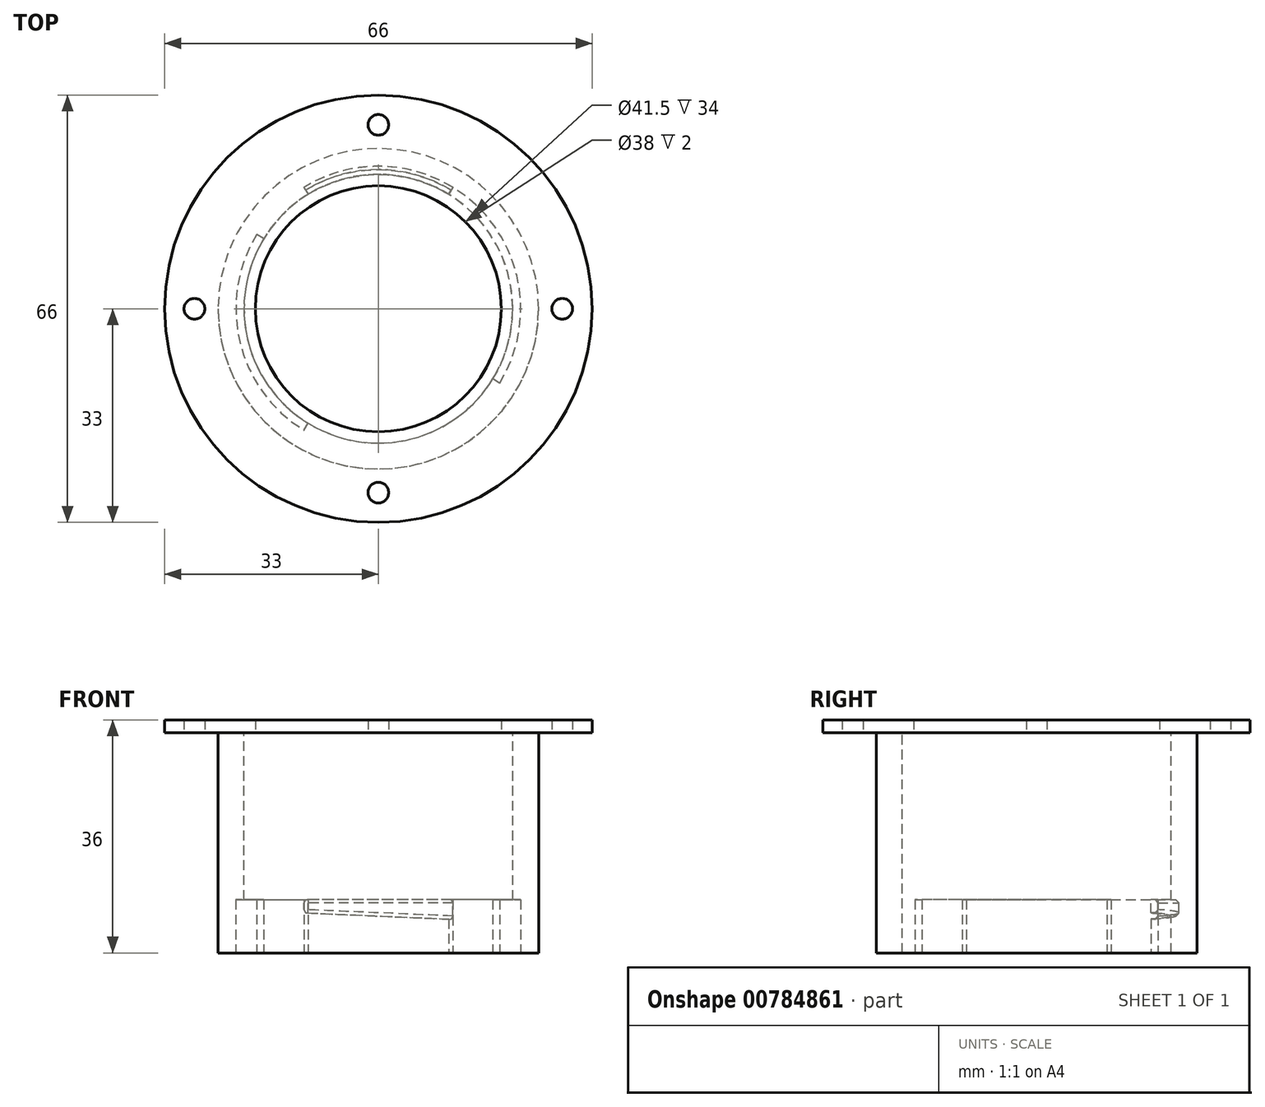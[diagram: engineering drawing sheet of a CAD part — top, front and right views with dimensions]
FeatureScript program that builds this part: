
annotation { "Feature Type Name" : "Feature", "Feature Type Description" : "" }
export const myFeature = defineFeature(function(context is Context, id is Id, definition is map)
    precondition{}
    {
        {
            var Q0;
            Q0=qCreatedBy(makeId("Top.planeOp"),FACE);
            var sketch = newSketch(context, id + "F0", { "sketchPlane" : qUnion([Q0])});
            skCircle(sketch, "E0", {"center": v(0, 0) * mm, "radius": 20.75 * mm});
            skCircle(sketch, "E1", {"center": v(0, 0) * mm, "radius": 18.75 * mm});
            skSolve(sketch);
        }
        {
            var Q0;
            Q0=makeQuery(id+"F0.imprint","IMPRINT",FACE,{"disambiguationData":[TD([[makeQuery(id+"F0.imprint","IMPRINT",EDGE,{"derivedFrom":sQuery(id+"F0.wireOp",EDGE,"E0")}),1.0]])]});
            extrude(context, id + "F1", {"entities" : qUnion([Q0]), "depth" : 34 * mm});
        }
        {
            var Q0;
            Q0=makeQuery(id+"F1.opExtrude","CAP_FACE",FACE,{"disambiguationData":[OSD([sQuery(id+"F0.wireOp",EDGE,"E0"),sQuery(id+"F0.wireOp",EDGE,"E1")])],"isStart":false});
            cPlane(context, id + "F2", {"entities" : qUnion([Q0]), "cplaneType" : CPlaneType.OFFSET, "offset" : 25.8 * mm, "oppositeDirection" : true, "width" : 150 * mm, "height" : 150 * mm});
        }
        {
            var Q0;
            Q0=qCreatedBy(id+"F2.planeOp",FACE);
            var sketch = newSketch(context, id + "F3", { "sketchPlane" : qUnion([Q0])});
            skCircle(sketch, "E2.0", {"center": v(0, 0) * mm, "radius": 20.75 * mm});
            skCircle(sketch, "E3", {"center": v(0, 0) * mm, "radius": 22 * mm});
            skLineSegment(sketch, "E4", {"start": v(-11.5, 18.75) * mm, "end": v(11.5, -18.75) * mm});
            skLineSegment(sketch, "E5", {"start": v(-11.5, -18.75) * mm, "end": v(11.5, 18.75) * mm});
            skLineSegment(sketch, "E6", {"start": v(-11.5, 18.75) * mm, "end": v(0, 21.22) * mm, "construction": true});
            skLineSegment(sketch, "E7", {"start": v(0, 21.22) * mm, "end": v(11.5, 18.75) * mm, "construction": true});
            skSolve(sketch);
        }
        {
            var Q0;
            {var subQ0=sQuery(id+"F3.wireOp",EDGE,"E4");var subQ1=sQuery(id+"F3.wireOp",EDGE,"E2.0");var subQ2=makeQuery(id+"F3.imprint","INTERSECT",VERTEX,{"disambiguationData":[OD(0.0)],"derivedFrom":[subQ1,subQ0]});Q0=makeQuery(id+"F3.imprint","IMPRINT",FACE,{"disambiguationData":[TD([[makeQuery(id+"F3.imprint","IMPRINT",EDGE,{"disambiguationData":[TD([[subQ2,1.0]])],"derivedFrom":subQ1}),-1.0]])]});}
            var Q1;
            {var subQ0=sQuery(id+"F3.wireOp",EDGE,"E5");var subQ1=sQuery(id+"F3.wireOp",EDGE,"E2.0");var subQ2=makeQuery(id+"F3.imprint","INTERSECT",VERTEX,{"disambiguationData":[OD(1.0)],"derivedFrom":[subQ1,subQ0]});Q1=makeQuery(id+"F3.imprint","IMPRINT",FACE,{"disambiguationData":[TD([[makeQuery(id+"F3.imprint","IMPRINT",EDGE,{"disambiguationData":[TD([[subQ2,-1.0]])],"derivedFrom":subQ1}),-1.0]])]});}
            extrude(context, id + "F4", {"entities" : qUnion([Q0, Q1]), "operationType" : NewBodyOperationType.ADD, "oppositeDirection" : true, "depth" : 3 * mm, "offsetDistance" : 25 * mm});
        }
        {
            var Q0;
            Q0=qCreatedBy(makeId("Front.planeOp"),FACE);
            cPlane(context, id + "F5", {"entities" : qUnion([Q0]), "cplaneType" : CPlaneType.OFFSET, "offset" : 25 * mm, "width" : 150 * mm, "height" : 150 * mm});
        }
        {
            var Q0;
            Q0=qCreatedBy(id+"F5.planeOp",FACE);
            var sketch = newSketch(context, id + "F6", { "sketchPlane" : qUnion([Q0])});
            skLineSegment(sketch, "E8.0.0", {"start": v(11.5, 8.2) * mm, "end": v(-11.5, 8.2) * mm});
            skLineSegment(sketch, "E8.0.1", {"start": v(-11.5, 8.2) * mm, "end": v(-11.5, 5.2) * mm});
            skLineSegment(sketch, "E8.0.2", {"start": v(-11.5, 5.2) * mm, "end": v(11.5, 5.2) * mm});
            skLineSegment(sketch, "E8.0.3", {"start": v(11.5, 5.2) * mm, "end": v(11.5, 8.2) * mm});
            skLineSegment(sketch, "E9", {"start": v(11.5, 6.2) * mm, "end": v(-11.5, 5.2) * mm});
            skSolve(sketch);
        }
        {
            var Q0;
            {var subQ0=sQuery(id+"F6.wireOp",EDGE,"E8.0.2");Q0=makeQuery(id+"F6.imprint","IMPRINT",FACE,{"disambiguationData":[TD([[makeQuery(id+"F6.imprint","IMPRINT",EDGE,{"derivedFrom":subQ0}),1.0]])]});}
            var Q1;
            Q1=makeQuery(id+"F1.opExtrude","SWEPT_FACE",FACE,{"disambiguationData":[OSD([sQuery(id+"F0.wireOp",EDGE,"E0")])]});
            extrude(context, id + "F7", {"entities" : qUnion([Q0]), "operationType" : NewBodyOperationType.REMOVE, "endBound" : BoundingType.UP_TO_SURFACE, "oppositeDirection" : true, "endBoundEntityFace" : qUnion([Q1]), "depth" : 25 * mm});
        }
        {
            var Q0;
            Q0=qCreatedBy(makeId("Front.planeOp"),FACE);
            cPlane(context, id + "F8", {"entities" : qUnion([Q0]), "cplaneType" : CPlaneType.OFFSET, "offset" : 25 * mm, "oppositeDirection" : true, "width" : 150 * mm, "height" : 150 * mm});
        }
        {
            var Q0;
            Q0=qCreatedBy(id+"F8.planeOp",FACE);
            var sketch = newSketch(context, id + "F9", { "sketchPlane" : qUnion([Q0])});
            skLineSegment(sketch, "E10.0.0", {"start": v(-11.5, 8.2) * mm, "end": v(11.5, 8.2) * mm});
            skLineSegment(sketch, "E10.0.1", {"start": v(11.5, 8.2) * mm, "end": v(11.5, 5.2) * mm});
            skLineSegment(sketch, "E10.0.2", {"start": v(11.5, 5.2) * mm, "end": v(-11.5, 5.2) * mm});
            skLineSegment(sketch, "E10.0.3", {"start": v(-11.5, 5.2) * mm, "end": v(-11.5, 8.2) * mm});
            skLineSegment(sketch, "E11", {"start": v(11.5, 5.2) * mm, "end": v(-11.5, 6.2) * mm});
            skSolve(sketch);
        }
        {
            var Q0;
            {var subQ0=sQuery(id+"F9.wireOp",EDGE,"E10.0.2");Q0=makeQuery(id+"F9.imprint","IMPRINT",FACE,{"disambiguationData":[TD([[makeQuery(id+"F9.imprint","IMPRINT",EDGE,{"derivedFrom":subQ0}),-1.0]])]});}
            var Q1;
            Q1=makeQuery(id+"F7.boolean.opBoolean","MERGE",FACE,{"derivedFrom":[makeQuery(id+"F1.opExtrude","SWEPT_FACE",FACE,{"disambiguationData":[OSD([sQuery(id+"F0.wireOp",EDGE,"E0")])]})],"fromTools":[makeQuery(id+"F7.opExtrude","CAP_FACE",FACE,{"disambiguationData":[OSD([sQuery(id+"F6.wireOp",EDGE,"E8.0.2"),sQuery(id+"F6.wireOp",EDGE,"E8.0.3"),sQuery(id+"F6.wireOp",EDGE,"E9")])],"isStart":false})]});
            extrude(context, id + "F10", {"entities" : qUnion([Q0]), "operationType" : NewBodyOperationType.REMOVE, "endBound" : BoundingType.UP_TO_SURFACE, "endBoundEntityFace" : qUnion([Q1]), "depth" : 25 * mm});
        }
        {
            var Q0;
            Q0=makeQuery(id+"F1.opExtrude","CAP_FACE",FACE,{"disambiguationData":[OSD([sQuery(id+"F0.wireOp",EDGE,"E0"),sQuery(id+"F0.wireOp",EDGE,"E1")])],"isStart":true});
            var sketch = newSketch(context, id + "F11", { "sketchPlane" : qUnion([Q0])});
            skCircle(sketch, "E12", {"center": v(0, 0) * mm, "radius": 24.25 * mm});
            skSolve(sketch);
        }
        {
            var Q0;
            Q0=makeQuery(id+"F11.imprint","IMPRINT",FACE,{"disambiguationData":[TD([[makeQuery(id+"F11.imprint","IMPRINT",EDGE,{"derivedFrom":sQuery(id+"F11.wireOp",EDGE,"E12")}),1.0]])]});
            var Q1;
            Q1=makeQuery(id+"F11.imprint","IMPRINT",FACE,{"disambiguationData":[TD([[makeQuery(id+"F11.imprint","IMPRINT",EDGE,{"derivedFrom":makeQuery(id+"F1.opExtrude","CAP_EDGE",EDGE,{"disambiguationData":[OSD([sQuery(id+"F0.wireOp",EDGE,"E0")])],"isStart":true})}),-1.0]])]});
            extrude(context, id + "F12", {"entities" : qUnion([Q0, Q1]), "operationType" : NewBodyOperationType.ADD, "depth" : 3 * mm});
        }
        {
            var Q0;
            Q0=makeQuery(id+"F12.opExtrude","CAP_FACE",FACE,{"disambiguationData":[OSD([sQuery(id+"F0.wireOp",EDGE,"E1"),sQuery(id+"F11.wireOp",EDGE,"E12")])],"isStart":false});
            var sketch = newSketch(context, id + "F13", { "sketchPlane" : qUnion([Q0])});
            skCircle(sketch, "E13.0", {"center": v(0, 0) * mm, "radius": 20.75 * mm});
            skCircle(sketch, "E14", {"center": v(0, 0) * mm, "radius": 16.75 * mm});
            skCircle(sketch, "E15.0", {"center": v(0, 0) * mm, "radius": 18.75 * mm});
            skSolve(sketch);
        }
        {
            var Q0;
            Q0=makeQuery(id+"F13.imprint","IMPRINT",FACE,{"disambiguationData":[TD([[makeQuery(id+"F13.imprint","IMPRINT",EDGE,{"derivedFrom":sQuery(id+"F13.wireOp",EDGE,"E14")}),-1.0]])]});
            extrude(context, id + "F14", {"entities" : qUnion([Q0]), "operationType" : NewBodyOperationType.ADD, "oppositeDirection" : true, "depth" : 3 * mm});
        }
        {
            var Q0;
            Q0=makeQuery(id+"F13.imprint","IMPRINT",FACE,{"disambiguationData":[TD([[makeQuery(id+"F13.imprint","IMPRINT",EDGE,{"derivedFrom":sQuery(id+"F13.wireOp",EDGE,"E13.0")}),1.0]])]});
            extrude(context, id + "F15", {"entities" : qUnion([Q0]), "operationType" : NewBodyOperationType.ADD, "depth" : 35 * mm});
        }
        {
            var Q0;
            Q0=makeQuery(id+"F1.opExtrude","CAP_EDGE",EDGE,{"disambiguationData":[OSD([sQuery(id+"F0.wireOp",EDGE,"E0")])],"isStart":false});
            var Q1;
            Q1=makeQuery(id+"F1.opExtrude","CAP_EDGE",EDGE,{"disambiguationData":[OSD([sQuery(id+"F0.wireOp",EDGE,"E1")])],"isStart":false});
            var Q2;
            {var subQ0=sQuery(id+"F3.wireOp",EDGE,"E3");Q2=makeQuery(id+"F4.opExtrude","CAP_EDGE",EDGE,{"disambiguationData":[OSD([subQ0]),TDD([makeQuery(id+"F3.imprint","IMPRINT",EDGE,{"disambiguationData":[TD([[makeQuery(id+"F3.imprint","INTERSECT",VERTEX,{"disambiguationData":[OD(1.0)],"derivedFrom":[subQ0,sQuery(id+"F3.wireOp",EDGE,"E4")]}),1.0]])],"derivedFrom":subQ0})])],"isStart":true});}
            var Q3;
            {var subQ0=sQuery(id+"F3.wireOp",EDGE,"E3");Q3=makeQuery(id+"F7.boolean.opBoolean","INTERSECT",EDGE,{"derivedFrom":[makeQuery(id+"F4.opExtrude","SWEPT_FACE",FACE,{"disambiguationData":[OSD([subQ0]),TDD([makeQuery(id+"F3.imprint","IMPRINT",EDGE,{"disambiguationData":[TD([[makeQuery(id+"F3.imprint","INTERSECT",VERTEX,{"disambiguationData":[OD(1.0)],"derivedFrom":[subQ0,sQuery(id+"F3.wireOp",EDGE,"E4")]}),1.0]])],"derivedFrom":subQ0})])]}),makeQuery(id+"F7.opExtrude","SWEPT_FACE",FACE,{"disambiguationData":[OSD([sQuery(id+"F6.wireOp",EDGE,"E9")])]})]});}
            var Q4;
            {var subQ0=sQuery(id+"F3.wireOp",EDGE,"E3");Q4=makeQuery(id+"F4.opExtrude","CAP_EDGE",EDGE,{"disambiguationData":[OSD([subQ0]),TDD([makeQuery(id+"F3.imprint","IMPRINT",EDGE,{"disambiguationData":[TD([[makeQuery(id+"F3.imprint","INTERSECT",VERTEX,{"disambiguationData":[OD(0.0)],"derivedFrom":[subQ0,sQuery(id+"F3.wireOp",EDGE,"E4")]}),1.0]])],"derivedFrom":subQ0})])],"isStart":true});}
            var Q5;
            {var subQ0=sQuery(id+"F3.wireOp",EDGE,"E3");Q5=makeQuery(id+"F10.boolean.opBoolean","INTERSECT",EDGE,{"derivedFrom":[makeQuery(id+"F4.opExtrude","SWEPT_FACE",FACE,{"disambiguationData":[OSD([subQ0]),TDD([makeQuery(id+"F3.imprint","IMPRINT",EDGE,{"disambiguationData":[TD([[makeQuery(id+"F3.imprint","INTERSECT",VERTEX,{"disambiguationData":[OD(0.0)],"derivedFrom":[subQ0,sQuery(id+"F3.wireOp",EDGE,"E4")]}),1.0]])],"derivedFrom":subQ0})])]}),makeQuery(id+"F10.opExtrude","SWEPT_FACE",FACE,{"disambiguationData":[OSD([sQuery(id+"F9.wireOp",EDGE,"E11")])]})]});}
            var Q6;
            Q6=makeQuery(id+"F1.opExtrude","CAP_EDGE",EDGE,{"disambiguationData":[OSD([sQuery(id+"F0.wireOp",EDGE,"E0")])],"isStart":true});
            chamfer(context, id + "F16", {"entities" : qUnion([Q0, Q1, Q2, Q3, Q4, Q5, Q6]), "width" : 0.5 * mm, "tangentPropagation" : true});
        }
        {
            var Q0;
            Q0=makeQuery(id+"F14.opExtrude","CAP_EDGE",EDGE,{"disambiguationData":[OSD([sQuery(id+"F13.wireOp",EDGE,"E14")])],"isStart":true});
            var Q1;
            Q1=makeQuery(id+"F14.opExtrude","CAP_EDGE",EDGE,{"disambiguationData":[OSD([sQuery(id+"F13.wireOp",EDGE,"E14")])],"isStart":false});
            var Q2;
            Q2=makeQuery(id+"F15.opExtrude","CAP_EDGE",EDGE,{"disambiguationData":[OSD([sQuery(id+"F13.wireOp",EDGE,"E13.0")])],"isStart":true});
            var Q3;
            Q3=makeQuery(id+"F12.opExtrude","CAP_EDGE",EDGE,{"disambiguationData":[OSD([sQuery(id+"F11.wireOp",EDGE,"E12")])],"isStart":false});
            var Q4;
            Q4=makeQuery(id+"F12.opExtrude","CAP_EDGE",EDGE,{"disambiguationData":[OSD([sQuery(id+"F11.wireOp",EDGE,"E12")])],"isStart":true});
            fillet(context, id + "F17", {"entities" : qUnion([Q0, Q1, Q2, Q3, Q4]), "radius" : 1.5 * mm, "tangentPropagation" : true, "allowEdgeOverflow" : false});
        }
        {
            var Q0;
            Q0=makeQuery(id+"F1.opExtrude","CAP_FACE",FACE,{"disambiguationData":[OSD([sQuery(id+"F0.wireOp",EDGE,"E0"),sQuery(id+"F0.wireOp",EDGE,"E1")])],"isStart":false});
            var sketch = newSketch(context, id + "F18", { "sketchPlane" : qUnion([Q0])});
            skCircle(sketch, "E16", {"center": v(0, 0) * mm, "radius": 24.75 * mm});
            skCircle(sketch, "E17.0", {"center": v(0, 0) * mm, "radius": 20.75 * mm});
            skSolve(sketch);
        }
        {
            var Q0;
            Q0=makeQuery(id+"F18.imprint","IMPRINT",FACE,{"disambiguationData":[TD([[makeQuery(id+"F18.imprint","IMPRINT",EDGE,{"derivedFrom":sQuery(id+"F18.wireOp",EDGE,"E16")}),1.0]])]});
            var Q1;
            Q1=makeQuery(id+"F12.opExtrude","CAP_FACE",FACE,{"disambiguationData":[OSD([sQuery(id+"F0.wireOp",EDGE,"E1"),sQuery(id+"F11.wireOp",EDGE,"E12")])],"isStart":true});
            extrude(context, id + "F19", {"entities" : qUnion([Q0]), "endBound" : BoundingType.UP_TO_SURFACE, "oppositeDirection" : true, "endBoundEntityFace" : qUnion([Q1]), "depth" : 35 * mm});
        }
        {
            var Q0;
            Q0=makeQuery(id+"F1.opExtrude","SWEPT_BODY",BODY,{"disambiguationData":[OSD([sQuery(id+"F0.wireOp",EDGE,"E0"),sQuery(id+"F0.wireOp",EDGE,"E1")])]});
            var Q1;
            Q1=makeQuery(id+"F19.opExtrude","SWEPT_BODY",BODY,{"disambiguationData":[OSD([sQuery(id+"F18.wireOp",EDGE,"E16"),sQuery(id+"F18.wireOp",EDGE,"E17.0")])]});
            booleanBodies(context, id + "F20", {"operationType" : BooleanOperationType.SUBTRACTION, "tools" : qUnion([Q0]), "targets" : qUnion([Q1])});
        }
        {
            var Q0;
            Q0=makeQuery(id+"F19.opExtrude","CAP_FACE",FACE,{"disambiguationData":[OSD([sQuery(id+"F18.wireOp",EDGE,"E16"),sQuery(id+"F18.wireOp",EDGE,"E17.0")])],"isStart":false});
            var sketch = newSketch(context, id + "F21", { "sketchPlane" : qUnion([Q0])});
            skLineSegment(sketch, "E18.0.0", {"start": v(-11.23, 18.32) * mm, "end": v(-10.85, 17.69) * mm});
            skLineSegment(sketch, "E18.0.2", {"start": v(-10.85, 17.69) * mm, "end": v(-11.24, 18.33) * mm});
            skLineSegment(sketch, "E18.0.3", {"start": v(-11.5, 18.75) * mm, "end": v(-11.24, 18.33) * mm});
            skFitSpline(sketch, "E18.0.5", {"points": [v(-11.5, 18.76) * mm, v(-11.41, 18.61) * mm, v(-11.32, 18.47) * mm, v(-11.23, 18.32) * mm]});
            skLineSegment(sketch, "E19.0.0", {"start": v(11.23, -18.32) * mm, "end": v(10.85, -17.69) * mm});
            skLineSegment(sketch, "E19.0.2", {"start": v(10.85, -17.69) * mm, "end": v(11.24, -18.33) * mm});
            skLineSegment(sketch, "E19.0.3", {"start": v(11.24, -18.33) * mm, "end": v(11.5, -18.75) * mm});
            skFitSpline(sketch, "E19.0.5", {"points": [v(11.5, -18.76) * mm, v(11.41, -18.61) * mm, v(11.32, -18.47) * mm, v(11.23, -18.32) * mm]});
            skCircle(sketch, "E20", {"center": v(0, 0) * mm, "radius": 20.75 * mm});
            skCircle(sketch, "E21", {"center": v(0, 0) * mm, "radius": 22 * mm});
            skLineSegment(sketch, "E22", {"start": v(18.76, 11.5) * mm, "end": v(0, 0) * mm});
            skLineSegment(sketch, "E23", {"start": v(0, 0) * mm, "end": v(-18.76, -11.5) * mm});
            skSolve(sketch);
        }
        {
            var Q0;
            {var subQ0=sQuery(id+"F21.wireOp",EDGE,"E19.0.5");var subQ3=makeQuery(id+"F21.imprint","IMPRINT",VERTEX,{"derivedFrom":subQ0});Q0=makeQuery(id+"F21.imprint","IMPRINT",FACE,{"disambiguationData":[TD([[makeQuery(id+"F21.imprint","IMPRINT",EDGE,{"disambiguationData":[TD([[subQ3,1.0]])],"derivedFrom":subQ0}),-1.0]])]});}
            var Q1;
            {var subQ0=sQuery(id+"F21.wireOp",EDGE,"E20");var subQ1=sQuery(id+"F21.wireOp",EDGE,"E19.0.2");var subQ2=makeQuery(id+"F21.imprint","INTERSECT",VERTEX,{"derivedFrom":[subQ1,subQ0]});Q1=makeQuery(id+"F21.imprint","IMPRINT",FACE,{"disambiguationData":[TD([[makeQuery(id+"F21.imprint","IMPRINT",EDGE,{"disambiguationData":[TD([[subQ2,-1.0]])],"derivedFrom":subQ0}),-1.0]])]});}
            var Q2;
            {var subQ1=sQuery(id+"F21.wireOp",EDGE,"E18.0.5");var subQ5=makeQuery(id+"F21.imprint","IMPRINT",VERTEX,{"derivedFrom":subQ1});Q2=makeQuery(id+"F21.imprint","IMPRINT",FACE,{"disambiguationData":[TD([[makeQuery(id+"F21.imprint","IMPRINT",EDGE,{"disambiguationData":[TD([[subQ5,1.0]])],"derivedFrom":subQ1}),-1.0]])]});}
            var Q3;
            {var subQ0=sQuery(id+"F21.wireOp",EDGE,"E20");var subQ1=sQuery(id+"F21.wireOp",EDGE,"E18.0.2");var subQ2=makeQuery(id+"F21.imprint","INTERSECT",VERTEX,{"derivedFrom":[subQ1,subQ0]});Q3=makeQuery(id+"F21.imprint","IMPRINT",FACE,{"disambiguationData":[TD([[makeQuery(id+"F21.imprint","IMPRINT",EDGE,{"disambiguationData":[TD([[subQ2,-1.0]])],"derivedFrom":subQ0}),-1.0]])]});}
            var Q4;
            {var subQ0=sQuery(id+"F3.wireOp",EDGE,"E5");var subQ1=sQuery(id+"F3.wireOp",EDGE,"E3");var subQ2=makeQuery(id+"F3.imprint","INTERSECT",VERTEX,{"disambiguationData":[OD(1.0)],"derivedFrom":[subQ1,subQ0]});var subQ3=sQuery(id+"F3.wireOp",EDGE,"E2.0");var subQ5=sQuery(id+"F3.wireOp",EDGE,"E4");var subQ6=makeQuery(id+"F3.imprint","INTERSECT",VERTEX,{"disambiguationData":[OD(0.0)],"derivedFrom":[subQ1,subQ5]});var subQ7=makeQuery(id+"F3.imprint","INTERSECT",VERTEX,{"disambiguationData":[OD(0.0)],"derivedFrom":[subQ3,subQ5]});Q4=makeQuery(id+"F20.opBoolean","COPY",FACE,{"derivedFrom":makeQuery(id+"F4.opExtrude","CAP_FACE",FACE,{"disambiguationData":[OSD([subQ3,subQ1,subQ5,subQ0]),TDD([makeQuery(id+"F3.imprint","IMPRINT",EDGE,{"disambiguationData":[TD([[subQ7,1.0]])],"derivedFrom":subQ3}),makeQuery(id+"F3.imprint","IMPRINT",EDGE,{"disambiguationData":[TD([[subQ6,1.0]])],"derivedFrom":subQ1}),makeQuery(id+"F3.imprint","IMPRINT",EDGE,{"disambiguationData":[TD([[subQ6,-1.0]])],"derivedFrom":subQ5}),makeQuery(id+"F3.imprint","IMPRINT",EDGE,{"disambiguationData":[TD([[subQ2,1.0]])],"derivedFrom":subQ0})])],"isStart":true})});}
            extrude(context, id + "F22", {"entities" : qUnion([Q0, Q1, Q2, Q3]), "operationType" : NewBodyOperationType.REMOVE, "endBound" : BoundingType.UP_TO_SURFACE, "oppositeDirection" : true, "endBoundEntityFace" : qUnion([Q4]), "depth" : 25 * mm, "offsetDistance" : 25 * mm});
        }
        {
            var Q0;
            Q0=makeQuery(id+"F19.opExtrude","CAP_FACE",FACE,{"disambiguationData":[OSD([sQuery(id+"F18.wireOp",EDGE,"E16"),sQuery(id+"F18.wireOp",EDGE,"E17.0")])],"isStart":true});
            var sketch = newSketch(context, id + "F23", { "sketchPlane" : qUnion([Q0])});
            skCircle(sketch, "E24.0", {"center": v(0, 0) * mm, "radius": 19 * mm});
            skCircle(sketch, "E25", {"center": v(0, 0) * mm, "radius": 33 * mm});
            skCircle(sketch, "E26", {"center": v(0, 0) * mm, "radius": 23 * mm});
            skCircle(sketch, "E27", {"center": v(0, 28.4) * mm, "radius": 1.6 * mm});
            skCircle(sketch, "E28", {"center": v(28.4, 0) * mm, "radius": 1.6 * mm});
            skCircle(sketch, "E29", {"center": v(0, -28.4) * mm, "radius": 1.6 * mm});
            skCircle(sketch, "E30", {"center": v(-28.4, 0) * mm, "radius": 1.6 * mm});
            skLineSegment(sketch, "E31", {"start": v(0, 28.4) * mm, "end": v(0, -28.4) * mm, "construction": true});
            skLineSegment(sketch, "E32", {"start": v(-28.4, 0) * mm, "end": v(28.4, 0) * mm, "construction": true});
            skCircle(sketch, "E33.0", {"center": v(0, 0) * mm, "radius": 20.75 * mm});
            skSolve(sketch);
        }
        {
            var Q0;
            Q0=makeQuery(id+"F23.imprint","IMPRINT",FACE,{"disambiguationData":[TD([[makeQuery(id+"F23.imprint","IMPRINT",EDGE,{"derivedFrom":sQuery(id+"F23.wireOp",EDGE,"E25")}),1.0]])]});
            var Q1;
            Q1=makeQuery(id+"F23.imprint","IMPRINT",FACE,{"disambiguationData":[TD([[makeQuery(id+"F23.imprint","IMPRINT",EDGE,{"derivedFrom":sQuery(id+"F23.wireOp",EDGE,"E26")}),-1.0]])]});
            var Q2;
            Q2=makeQuery(id+"F23.imprint","IMPRINT",FACE,{"disambiguationData":[TD([[makeQuery(id+"F23.imprint","IMPRINT",EDGE,{"derivedFrom":sQuery(id+"F23.wireOp",EDGE,"E26")}),1.0]])]});
            var Q3;
            Q3=makeQuery(id+"F23.imprint","IMPRINT",FACE,{"disambiguationData":[TD([[makeQuery(id+"F23.imprint","IMPRINT",EDGE,{"derivedFrom":sQuery(id+"F23.wireOp",EDGE,"E24.0")}),-1.0]])]});
            extrude(context, id + "F24", {"entities" : qUnion([Q0, Q1, Q2, Q3]), "operationType" : NewBodyOperationType.ADD, "depth" : 2 * mm, "offsetDistance" : 25 * mm});
        }
    });
